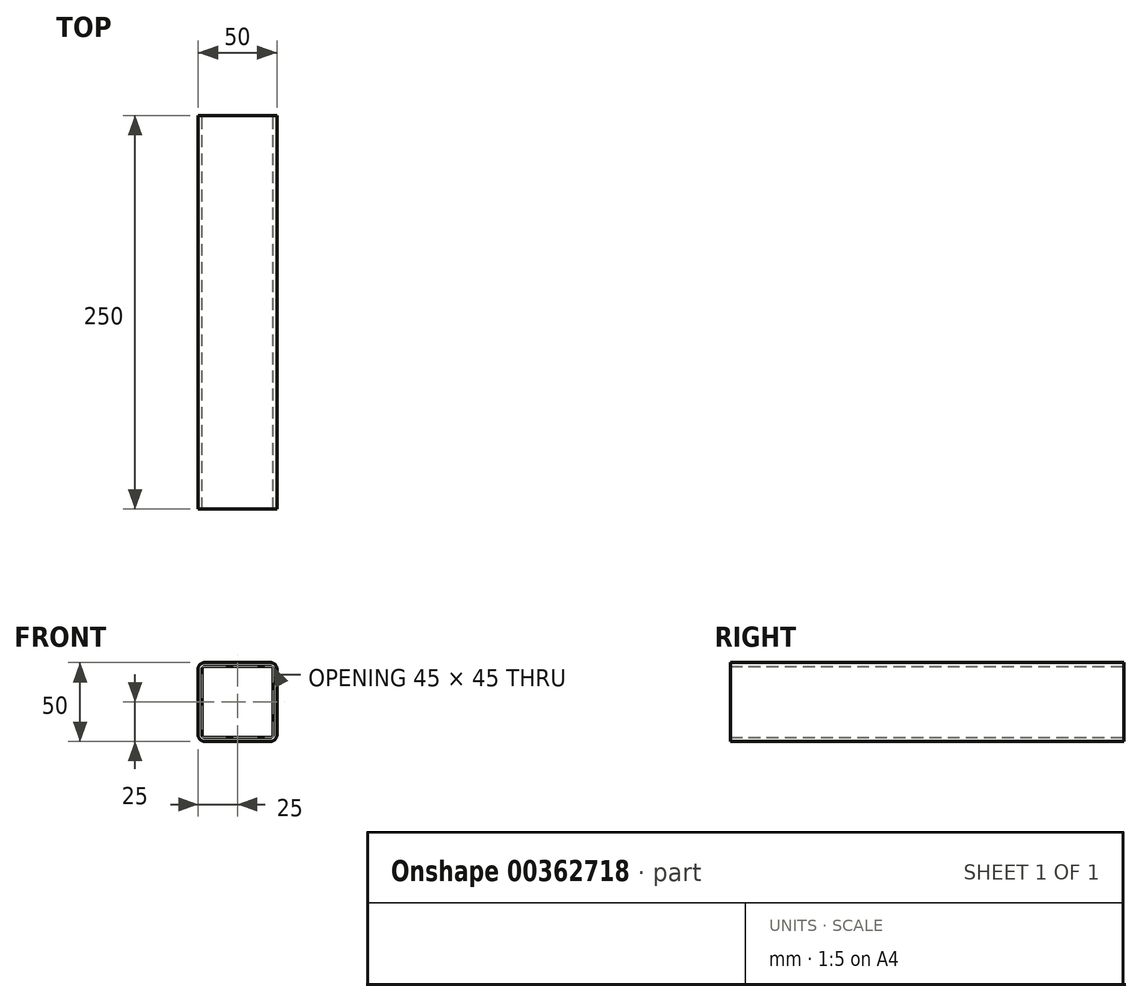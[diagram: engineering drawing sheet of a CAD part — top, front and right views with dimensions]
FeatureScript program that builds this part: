
annotation { "Feature Type Name" : "Feature", "Feature Type Description" : "" }
export const myFeature = defineFeature(function(context is Context, id is Id, definition is map)
    precondition{}
    {
        {
            var Q0;
            Q0=qCreatedBy(makeId("Front.planeOp"),FACE);
            var sketch = newSketch(context, id + "F0", { "sketchPlane" : qUnion([Q0])});
            skLineSegment(sketch, "E0.bottom", {"start": v(-21, 25) * mm, "end": v(21, 25) * mm});
            skLineSegment(sketch, "E0.top", {"start": v(-21, -25) * mm, "end": v(21, -25) * mm});
            skLineSegment(sketch, "E0.left", {"start": v(-25, 21) * mm, "end": v(-25, -21) * mm});
            skLineSegment(sketch, "E0.right", {"start": v(25, 21) * mm, "end": v(25, -21) * mm});
            skPoint(sketch, "E0.middle", {"position": v(0, 0) * mm});
            skPoint(sketch, "E1.visualSharp", {"position": v(-24, 24) * mm});
            skPoint(sketch, "E2.visualSharp", {"position": v(-25, 25) * mm});
            skArc(sketch, "E2.filletArc", {"start": v(-21, 25) * mm, "mid": v(-23.83, 23.83) * mm, "end": v(-25, 21) * mm});
            skPoint(sketch, "E3.visualSharp", {"position": v(24, 24) * mm});
            skPoint(sketch, "E4.visualSharp", {"position": v(25, 25) * mm});
            skArc(sketch, "E4.filletArc", {"start": v(25, 21) * mm, "mid": v(23.83, 23.83) * mm, "end": v(21, 25) * mm});
            skPoint(sketch, "E5.visualSharp", {"position": v(24, -24) * mm});
            skPoint(sketch, "E6.visualSharp", {"position": v(-24, -24) * mm});
            skPoint(sketch, "E7.visualSharp", {"position": v(-25, -25) * mm});
            skArc(sketch, "E7.filletArc", {"start": v(-25, -21) * mm, "mid": v(-23.83, -23.83) * mm, "end": v(-21, -25) * mm});
            skPoint(sketch, "E8.visualSharp", {"position": v(25, -25) * mm});
            skArc(sketch, "E8.filletArc", {"start": v(21, -25) * mm, "mid": v(23.83, -23.83) * mm, "end": v(25, -21) * mm});
            skArc(sketch, "E9.0", {"start": v(-21, 22.5) * mm, "mid": v(-22.06, 22.06) * mm, "end": v(-22.5, 21) * mm});
            skLineSegment(sketch, "E9.1", {"start": v(-22.5, 21) * mm, "end": v(-22.5, -21) * mm});
            skLineSegment(sketch, "E9.2", {"start": v(-21, 22.5) * mm, "end": v(21, 22.5) * mm});
            skArc(sketch, "E9.3", {"start": v(-22.5, -21) * mm, "mid": v(-22.06, -22.06) * mm, "end": v(-21, -22.5) * mm});
            skArc(sketch, "E9.4", {"start": v(22.5, 21) * mm, "mid": v(22.06, 22.06) * mm, "end": v(21, 22.5) * mm});
            skLineSegment(sketch, "E9.5", {"start": v(22.5, 21) * mm, "end": v(22.5, -21) * mm});
            skArc(sketch, "E9.6", {"start": v(21, -22.5) * mm, "mid": v(22.06, -22.06) * mm, "end": v(22.5, -21) * mm});
            skLineSegment(sketch, "E9.7", {"start": v(-21, -22.5) * mm, "end": v(21, -22.5) * mm});
            skSolve(sketch);
        }
        {
            var Q0;
            Q0 = qSketchRegion(id + "F0", true);
            var Q1;
            Q1=makeQuery(id+"F0.imprint","IMPRINT",FACE,{"disambiguationData":[TD([[makeQuery(id+"F0.imprint","IMPRINT",EDGE,{"derivedFrom":sQuery(id+"F0.wireOp",EDGE,"NPTbhyxs-uorz-5i4G-Ztf1-AYHWqOiu6JAR")}),1.0]])]});
            extrude(context, id + "F1", {"entities" : qUnion([Q0, Q1]), "offsetDistance" : 25 * mm, "depth" : 250 * mm});
        }
    });
